# Revit family: SonoMeter40_DN25_RFA
name_source: partatom
category: Pipe Accessories
revit_build: Autodesk Revit 2017 (Build: 20161205_1400(x64)
units: mm (PartAtom-declared; Revit-internal decimal feet)

## family parameters
Always vertical = Yes
Cut with Voids When Loaded = No
Part Type = Valve - Breaks Into
Round Connector Dimension = Use Diameter
Shared = No
Work Plane-Based = No

## types (2) — shared parameters
A = 45.00°
A_H = 79 mm
A_H1 = 40 mm
Body Material = Danfoss Brass
Connection = G1¼B
D = 25 mm  [stored 0.082021 ft]
D1 = 38 mm  [stored 0.124672 ft]
D2 = 42 mm
D3 = 33 mm
D4 = 34 mm
D5 = 49 mm
D6 = 36 mm
Description = Energy Meter
H = 69 mm
IfcExportAs = IfcValveType
IfcExportType = SonoMeter 40
L = 260 mm  [stored 0.853018 ft]
L-1 = 11 mm  [stored 0.0360892 ft]
L1 = 281 mm
L1-1 = 19 mm  [stored 0.062336 ft]
L2 = 361 mm
L2-1 = 57 mm
L3 = 84 mm
L4 = 18 mm  [stored 0.0590551 ft]
L5 = 15 mm  [stored 0.0492126 ft]
L6 = 22 mm  [stored 0.0721785 ft]
L7 = 30 mm  [stored 0.0984252 ft]
L8 = 10 mm  [stored 0.0328084 ft]
L9 = 24 mm
LOD 200 = No
LOD 350 = Yes
Lnut = 20 mm  [stored 0.0656168 ft]
Manufacturer = Danfoss
Model = SonoMeter 40
Operation Pressure = PN25
URL = https://store.danfoss.com
Weight = 3.20 kg

## per-type parameters (varying)
| type | Kvs | Max Flow | Min Flow | Nominal Flow |
| SonoMeter40_DN25_G1¼_Kvs11.67_260mm | 11.7 m³/h | 7 m3/h | 0.035 m3/h | 3.5 m3/h |
| SonoMeter40_DN25_G1¼_Kvs18.97_260mm | 19.0 m³/h | 12 m3/h | 0.06 m3/h | 6.0 m3/h |

note: column(s) folded — value = type name in every type: Model Type

note: [stored X ft] marks values corroborated as IEEE doubles in the binary element streams (Revit-internal decimal feet)

## geometry (parser evidence)
native form markers: Sweep x8
no freeform markers — native parametric forms only
